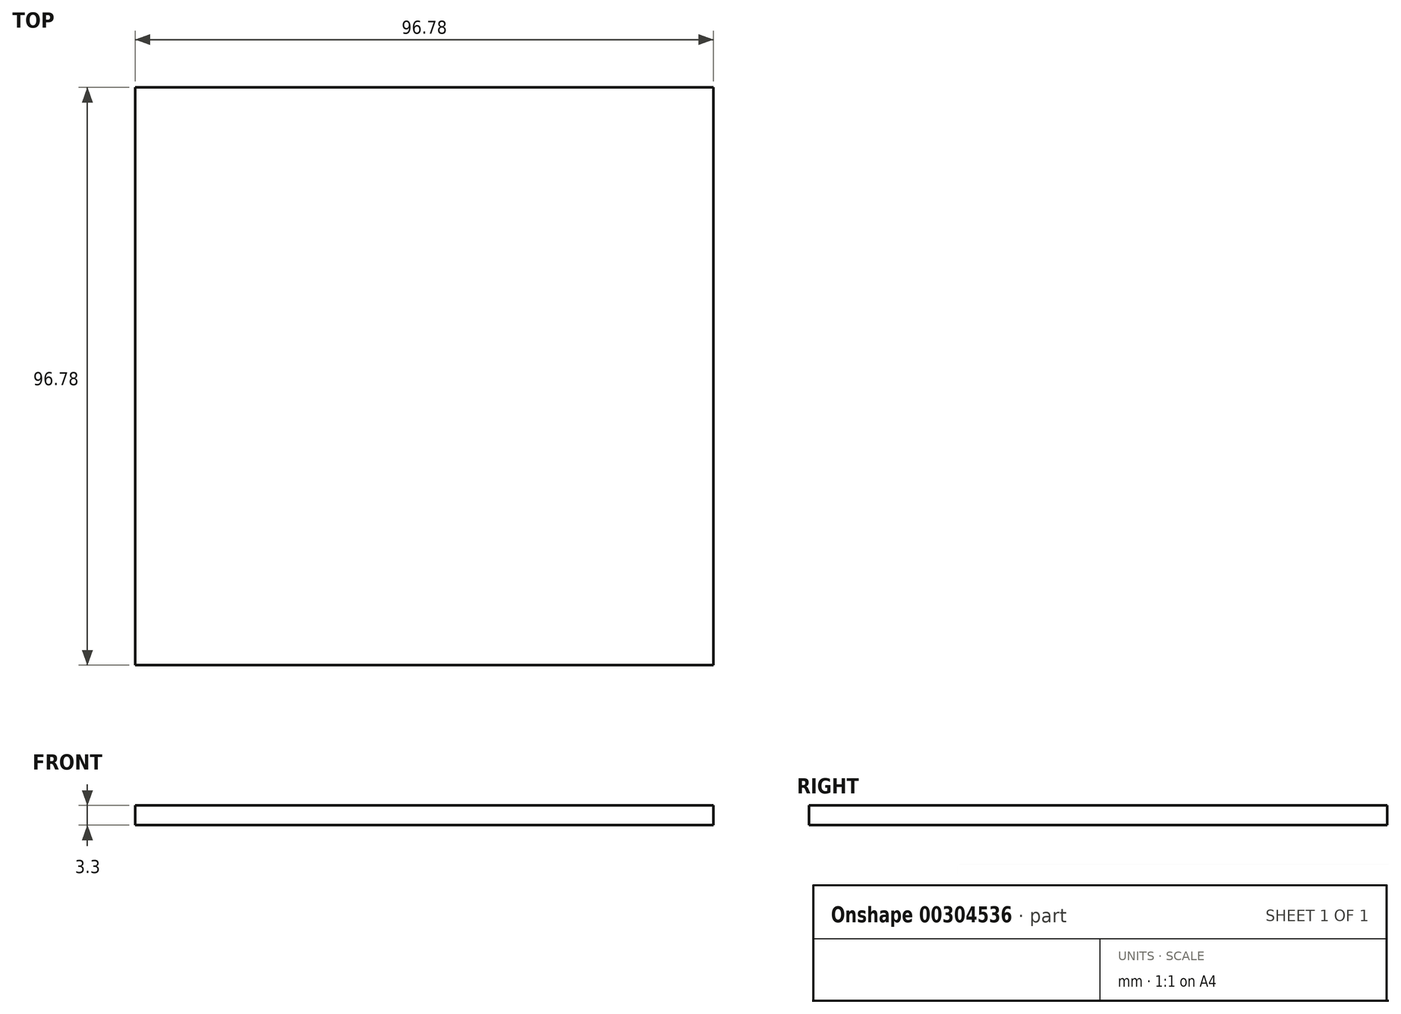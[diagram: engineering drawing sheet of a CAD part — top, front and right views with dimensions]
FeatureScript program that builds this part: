
annotation { "Feature Type Name" : "Feature", "Feature Type Description" : "" }
export const myFeature = defineFeature(function(context is Context, id is Id, definition is map)
    precondition{}
    {
        {
            var Q0;
            Q0=qCreatedBy(makeId("Top.planeOp"),FACE);
            var sketch = newSketch(context, id + "F0", { "sketchPlane" : qUnion([Q0])});
            skLineSegment(sketch, "E0.bottom", {"start": v(48.39, 48.39) * mm, "end": v(-48.39, 48.39) * mm});
            skLineSegment(sketch, "E0.top", {"start": v(48.39, -48.39) * mm, "end": v(-48.39, -48.39) * mm});
            skLineSegment(sketch, "E0.left", {"start": v(48.39, 48.39) * mm, "end": v(48.39, -48.39) * mm});
            skLineSegment(sketch, "E0.right", {"start": v(-48.39, 48.39) * mm, "end": v(-48.39, -48.39) * mm});
            skPoint(sketch, "E0.middle", {"position": v(0, 0) * mm});
            skSolve(sketch);
        }
        {
            var Q0;
            Q0 = qSketchRegion(id + "F0", true);
            extrude(context, id + "F1", {"entities" : qUnion([Q0]), "depth" : 3.3 * mm});
        }
    });
